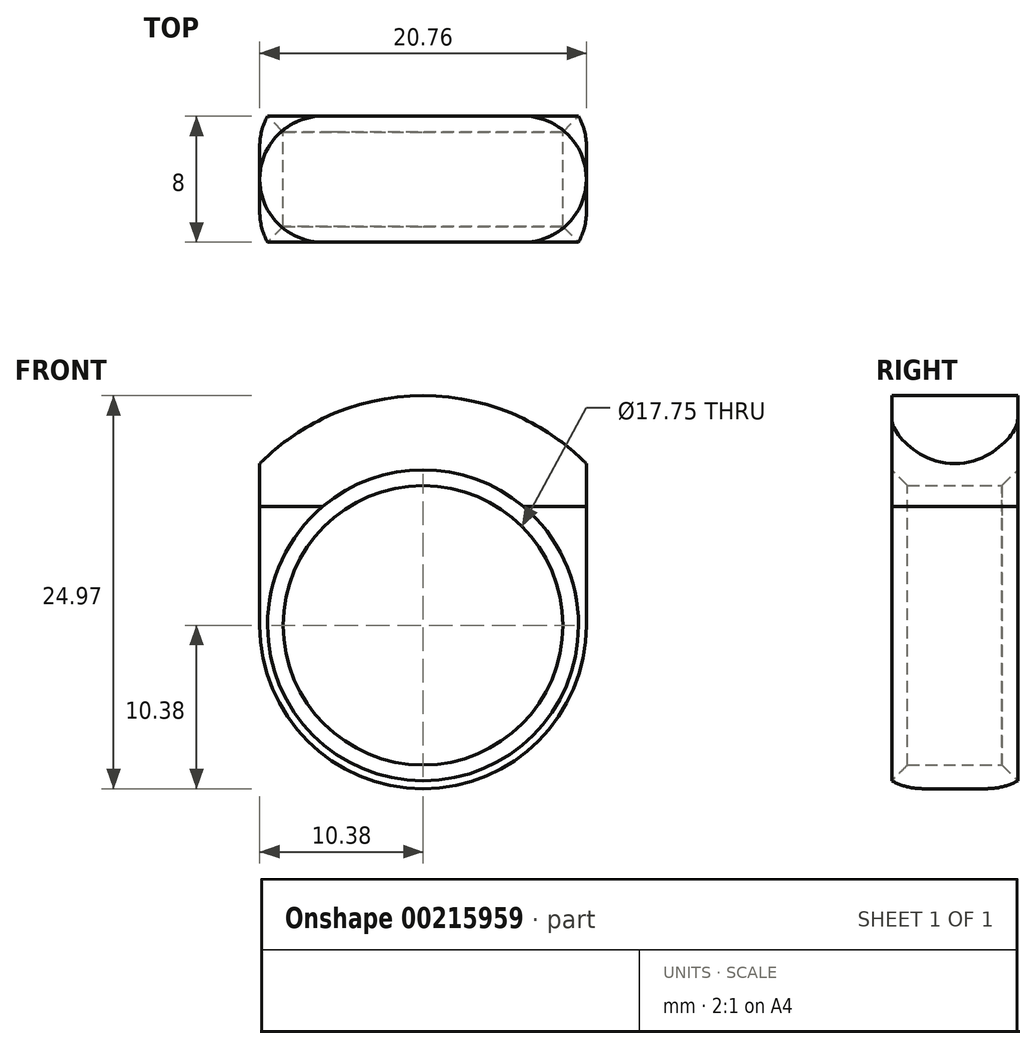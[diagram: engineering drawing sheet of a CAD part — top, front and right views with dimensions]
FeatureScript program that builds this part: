
annotation { "Feature Type Name" : "Feature", "Feature Type Description" : "" }
export const myFeature = defineFeature(function(context is Context, id is Id, definition is map)
    precondition{}
    {
        {
            var Q0;
            Q0=qCreatedBy(makeId("Front.planeOp"),FACE);
            var sketch = newSketch(context, id + "F0", { "sketchPlane" : qUnion([Q0])});
            skCircle(sketch, "E0", {"center": v(0, 0) * mm, "radius": 8.88 * mm});
            skCircle(sketch, "E1.0", {"center": v(0, 0) * mm, "radius": 10.38 * mm});
            skCircle(sketch, "E2.0", {"center": v(0, 0) * mm, "radius": 20.38 * mm});
            skLineSegment(sketch, "E3", {"start": v(10.38, 0) * mm, "end": v(10.38, 17.54) * mm});
            skLineSegment(sketch, "E4.MirrorCS", {"start": v(-10.38, 0) * mm, "end": v(-10.38, 17.54) * mm});
            skCircle(sketch, "E5.0", {"center": v(0, 0) * mm, "radius": 19.38 * mm});
            skLineSegment(sketch, "E6", {"start": v(-0.5, 20.37) * mm, "end": v(-0.5, 19.37) * mm});
            skLineSegment(sketch, "E7.MirrorCS", {"start": v(0.5, 20.37) * mm, "end": v(0.5, 19.37) * mm});
            skLineSegment(sketch, "E8", {"start": v(0, 20.38) * mm, "end": v(0, 19.38) * mm});
            skArc(sketch, "E9", {"start": v(10.37, 10.26) * mm, "mid": v(0, 14.6) * mm, "end": v(-10.38, 10.26) * mm});
            skLineSegment(sketch, "E10", {"start": v(0, 19.38) * mm, "end": v(0, 14.6) * mm});
            skSolve(sketch);
        }
        {
            var Q0;
            Q0=makeQuery(id+"F0.imprint","IMPRINT",FACE,{"disambiguationData":[TD([[makeQuery(id+"F0.imprint","IMPRINT",EDGE,{"derivedFrom":sQuery(id+"F0.wireOp",EDGE,"E0")}),-1.0]])]});
            extrude(context, id + "F1", {"entities" : qUnion([Q0]), "depth" : 4 * mm, "hasSecondDirection" : true, "secondDirectionOppositeDirection" : true, "secondDirectionDepth" : 4 * mm});
        }
        {
            var Q0;
            Q0=makeQuery(id+"F1.opExtrude","CAP_EDGE",EDGE,{"disambiguationData":[OSD([sQuery(id+"F0.wireOp",EDGE,"E0")])],"isStart":false});
            var Q1;
            Q1=makeQuery(id+"F1.opExtrude","CAP_EDGE",EDGE,{"disambiguationData":[OSD([sQuery(id+"F0.wireOp",EDGE,"E0")])],"isStart":true});
            chamfer(context, id + "F2", {"entities" : qUnion([Q0, Q1]), "width" : 1 * mm, "tangentPropagation" : true});
        }
        {
            var Q0;
            {var subQ0=sQuery(id+"F0.wireOp",EDGE,"E3");var subQ1=sQuery(id+"F0.wireOp",EDGE,"E1.0");var subQ2=makeQuery(id+"F0.imprint","INTERSECT",VERTEX,{"derivedFrom":[subQ1,subQ0]});Q0=makeQuery(id+"F0.imprint","IMPRINT",FACE,{"disambiguationData":[TD([[makeQuery(id+"F0.imprint","IMPRINT",EDGE,{"disambiguationData":[TD([[subQ2,-1.0]])],"derivedFrom":subQ1}),-1.0]])]});}
            extrude(context, id + "F3", {"entities" : qUnion([Q0]), "operationType" : NewBodyOperationType.ADD, "depth" : 4 * mm, "hasSecondDirection" : true, "secondDirectionOppositeDirection" : true, "secondDirectionDepth" : 4 * mm});
        }
        {
            var Q0;
            Q0=makeQuery(id+"F3.opExtrude","CAP_EDGE",EDGE,{"disambiguationData":[OSD([sQuery(id+"F0.wireOp",EDGE,"E3")])],"isStart":false});
            var Q1;
            Q1=makeQuery(id+"F3.opExtrude","CAP_EDGE",EDGE,{"disambiguationData":[OSD([sQuery(id+"F0.wireOp",EDGE,"E3")])],"isStart":true});
            var Q2;
            Q2=makeQuery(id+"F3.opExtrude","CAP_EDGE",EDGE,{"disambiguationData":[OSD([sQuery(id+"F0.wireOp",EDGE,"E4.MirrorCS")])],"isStart":false});
            var Q3;
            Q3=makeQuery(id+"F3.opExtrude","CAP_EDGE",EDGE,{"disambiguationData":[OSD([sQuery(id+"F0.wireOp",EDGE,"E4.MirrorCS")])],"isStart":true});
            fillet(context, id + "F4", {"entities" : qUnion([Q0, Q1, Q2, Q3]), "radius" : 4 * mm, "tangentPropagation" : true, "allowEdgeOverflow" : false});
        }
    });
